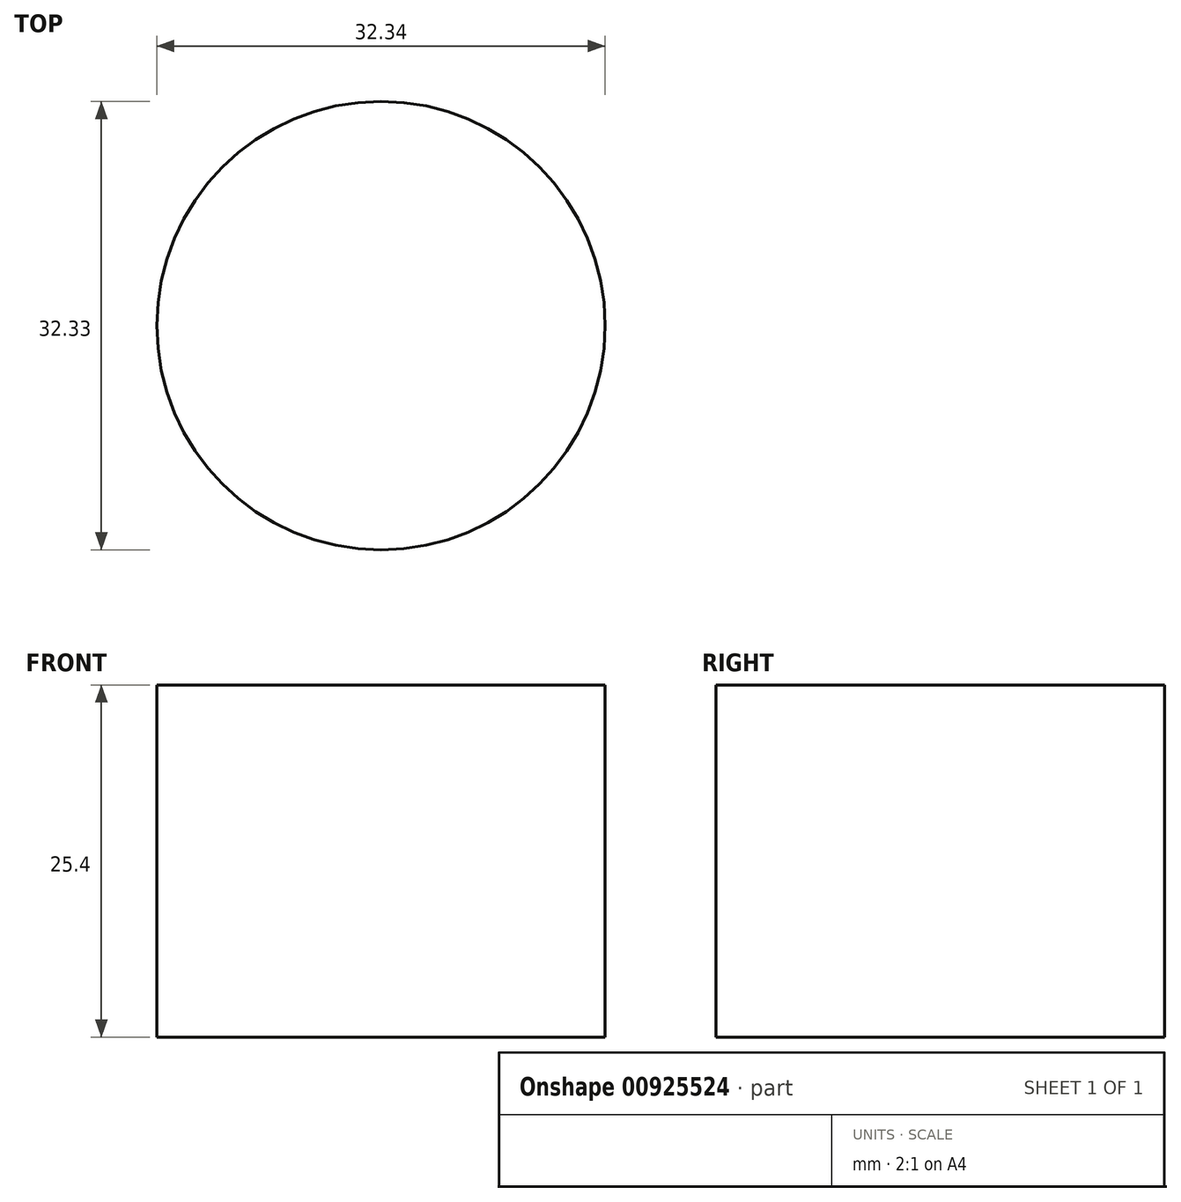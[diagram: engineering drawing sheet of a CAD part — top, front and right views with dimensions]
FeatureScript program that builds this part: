
annotation { "Feature Type Name" : "Feature", "Feature Type Description" : "" }
export const myFeature = defineFeature(function(context is Context, id is Id, definition is map)
    precondition{}
    {
        {
            var Q0;
            Q0=qCreatedBy(makeId("Top.planeOp"),FACE);
            var sketch = newSketch(context, id + "F0", { "sketchPlane" : qUnion([Q0])});
            skCircle(sketch, "E0", {"center": v(0, 27.93) * mm, "radius": 16.17 * mm});
            skSolve(sketch);
        }
        {
            var Q0;
            Q0 = qSketchRegion(id + "F0", true);
            extrude(context, id + "F1", {"entities" : qUnion([Q0]), "depth" : 25.4 * mm, "offsetDistance" : 25.4 * mm});
        }
    });
